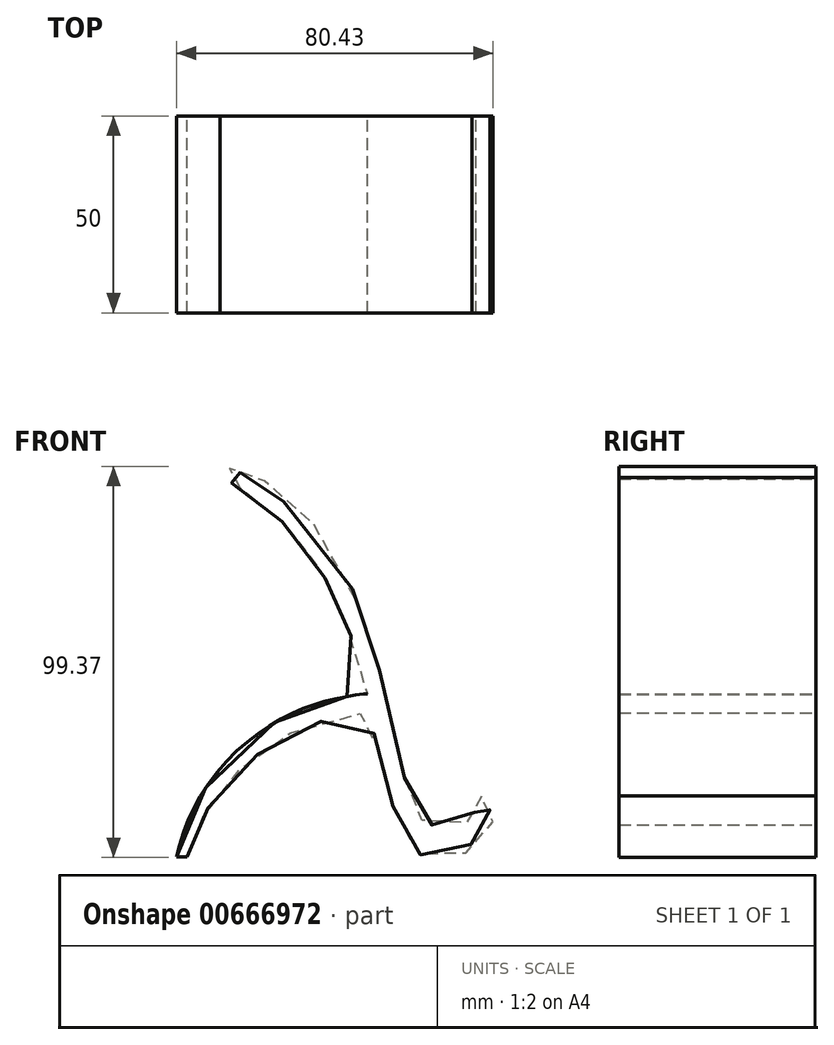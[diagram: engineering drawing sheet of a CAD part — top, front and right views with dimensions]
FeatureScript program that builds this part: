
annotation { "Feature Type Name" : "Feature", "Feature Type Description" : "" }
export const myFeature = defineFeature(function(context is Context, id is Id, definition is map)
    precondition{}
    {
        {
            var Q0;
            Q0=qCreatedBy(makeId("Front.planeOp"),FACE);
            var sketch = newSketch(context, id + "F0", { "sketchPlane" : qUnion([Q0])});
            skLineSegment(sketch, "E0", {"start": v(9.29, 8.16) * mm, "end": v(11.95, 8.16) * mm});
            skFitSpline(sketch, "E1", {"points": [v(11.95, 8.16) * mm, v(12.67, 10.19) * mm, v(13.9, 13.64) * mm, v(15.55, 17.39) * mm, v(18.72, 22.93) * mm, v(22.9, 28.04) * mm, v(28.94, 33.51) * mm, v(34.2, 37.4) * mm, v(40.71, 40.85) * mm, v(48.45, 43.3) * mm, v(58.43, 44.72) * mm, v(58.63, 44.31) * mm, v(59.45, 39.94) * mm, v(60.52, 35.46) * mm, v(63.15, 24.66) * mm, v(64.8, 19.7) * mm, v(66.8, 15.33) * mm, v(69, 12.46) * mm, v(71.16, 8.8) * mm, v(76.54, 8.16) * mm, v(80.18, 8.16) * mm, v(83.62, 10.04) * mm, v(84.9, 13.1) * mm, v(87.7, 14.65) * mm, v(89.71, 17.33) * mm, v(88.91, 18.84) * mm, v(88.87, 21) * mm, v(87.94, 22.25) * mm, v(87.18, 23.62) * mm, v(85.88, 23.14) * mm, v(84.36, 21.9) * mm, v(85.32, 18.13) * mm, v(83.47, 16.97) * mm, v(81.08, 16.48) * mm, v(76.04, 16.33) * mm, v(72.31, 16.94) * mm, v(69.73, 21.6) * mm, v(68.31, 25.22) * mm, v(66.6, 30.3) * mm, v(62.3, 49.06) * mm, v(59.4, 61.05) * mm, v(56.24, 70.66) * mm, v(51.78, 80.88) * mm, v(39.26, 97.32) * mm, v(33.26, 100.02) * mm, v(30.97, 104.47) * mm, v(26.35, 104.35) * mm, v(24.75, 107.26) * mm, v(22.35, 106.74) * mm, v(20.43, 105.42) * mm, v(20.64, 104.52) * mm, v(22.5, 103.62) * mm, v(26.06, 101.58) * mm, v(30.87, 98.25) * mm, v(34.53, 95.06) * mm, v(41.07, 88.1) * mm, v(43.37, 85.04) * mm, v(47.2, 78.85) * mm, v(50, 73.25) * mm, v(52.03, 68.31) * mm, v(53.81, 63.83) * mm, v(57.77, 49.6) * mm, v(57.3, 49.6) * mm, v(52.98, 49.05) * mm, v(45.9, 47.42) * mm, v(38.32, 44.52) * mm, v(29.35, 39.05) * mm, v(20.2, 30.48) * mm, v(13.3, 19.9) * mm, v(10.5, 12.56) * mm, v(9.29, 8.16) * mm], "startDerivative": vector(66.28, 227) * mm, "endDerivative": vector(-76.18, -326.2) * mm});
            skLineSegment(sketch, "E2", {"start": v(9.29, 8.16) * mm, "end": v(94.16, 8.16) * mm, "construction": true});
            skSolve(sketch);
        }
        {
            var Q0;
            Q0=makeQuery(id+"F0.imprint","IMPRINT",FACE,{"disambiguationData":[TD([[makeQuery(id+"F0.imprint","IMPRINT",EDGE,{"derivedFrom":sQuery(id+"F0.wireOp",EDGE,"E0")}),1.0]])]});
            extrude(context, id + "F1", {"entities" : qUnion([Q0]), "depth" : 50 * mm, "offsetDistance" : 25 * mm});
        }
    });
